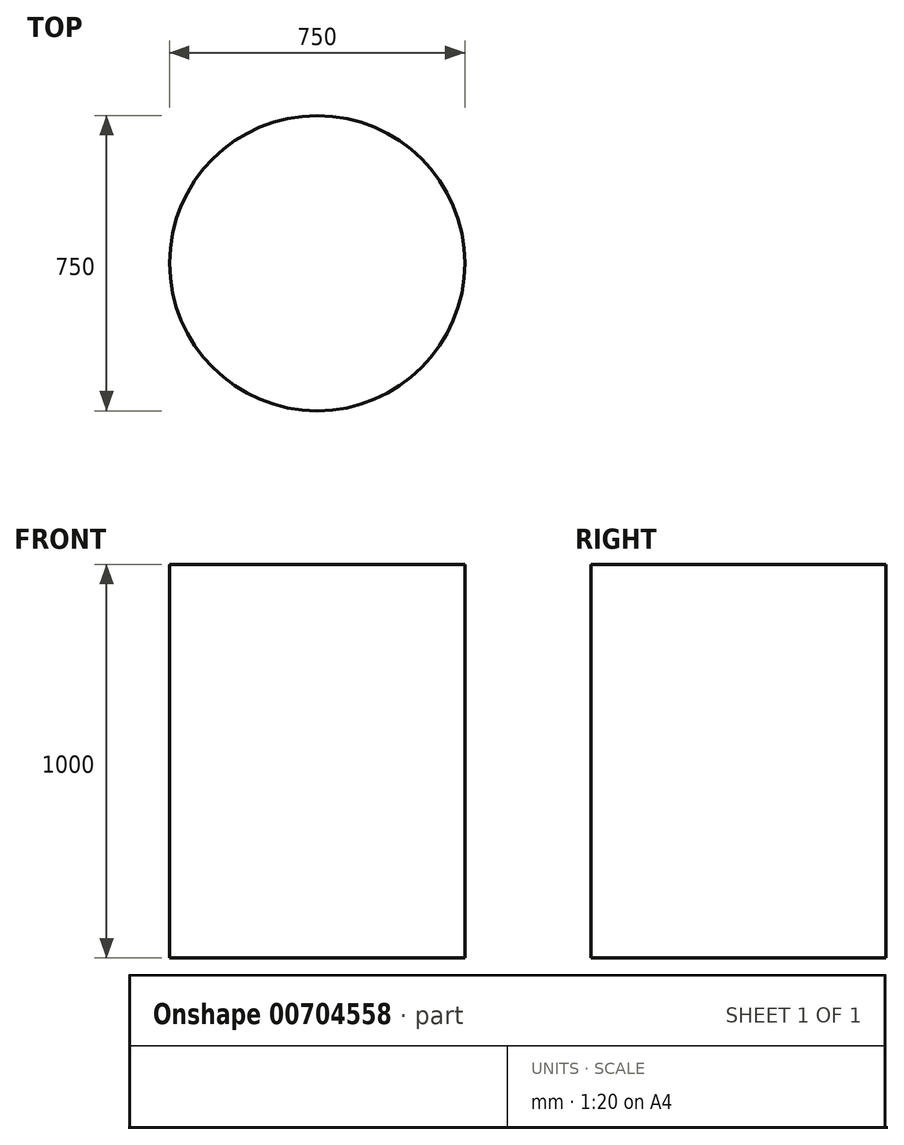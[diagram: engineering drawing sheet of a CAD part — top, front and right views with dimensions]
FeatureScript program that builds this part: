
annotation { "Feature Type Name" : "Feature", "Feature Type Description" : "" }
export const myFeature = defineFeature(function(context is Context, id is Id, definition is map)
    precondition{}
    {
        {
            var Q0;
            Q0=qCreatedBy(makeId("Top.planeOp"),FACE);
            var sketch = newSketch(context, id + "F0", { "sketchPlane" : qUnion([Q0])});
            skCircle(sketch, "E0", {"center": v(0, 0) * mm, "radius": 375 * mm});
            skSolve(sketch);
        }
        {
            var Q0;
            Q0=makeQuery(id+"F0.imprint","IMPRINT",FACE,{"disambiguationData":[TD([[makeQuery(id+"F0.imprint","IMPRINT",EDGE,{"derivedFrom":sQuery(id+"F0.wireOp",EDGE,"E0")}),1.0]])]});
            extrude(context, id + "F1", {"entities" : qUnion([Q0]), "depth" : 1000 * mm, "offsetDistance" : 25 * mm});
        }
    });
